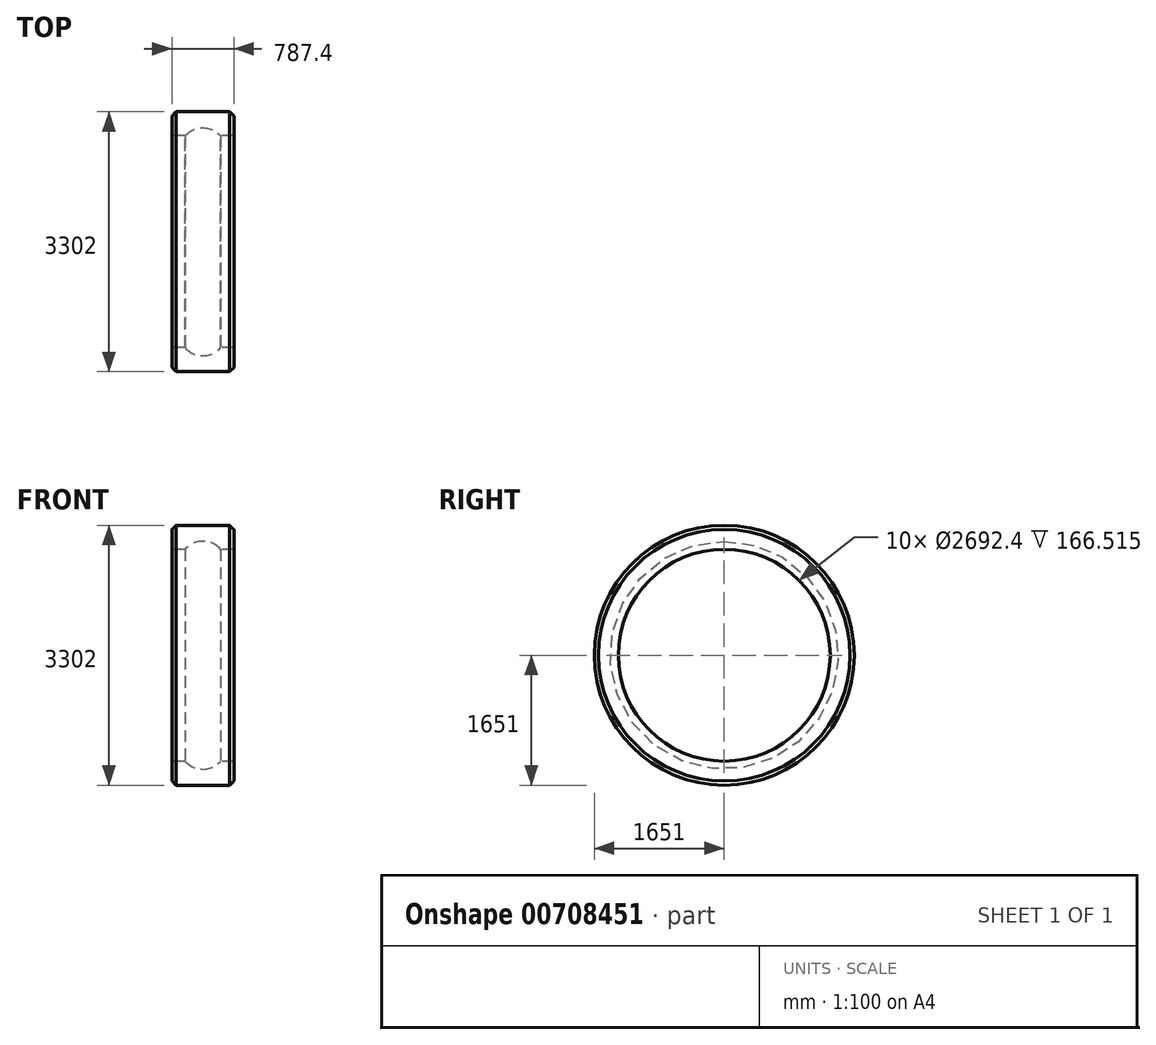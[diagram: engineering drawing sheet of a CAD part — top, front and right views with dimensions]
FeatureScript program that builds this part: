
annotation { "Feature Type Name" : "Feature", "Feature Type Description" : "" }
export const myFeature = defineFeature(function(context is Context, id is Id, definition is map)
    precondition{}
    {
        {
            var Q0;
            Q0=qCreatedBy(makeId("Front.planeOp"),FACE);
            var sketch = newSketch(context, id + "F0", { "sketchPlane" : qUnion([Q0])});
            skLineSegment(sketch, "E0", {"start": v(-565.35, 0) * mm, "end": v(3267.77, 0) * mm});
            skLineSegment(sketch, "E1.bottom", {"start": v(-393.7, 1346.2) * mm, "end": v(-227.18, 1346.2) * mm});
            skLineSegment(sketch, "E1.top", {"start": v(-393.7, 1651) * mm, "end": v(393.7, 1651) * mm});
            skLineSegment(sketch, "E1.left", {"start": v(-393.7, 1346.2) * mm, "end": v(-393.7, 1651) * mm});
            skLineSegment(sketch, "E1.right", {"start": v(393.7, 1346.2) * mm, "end": v(393.7, 1651) * mm});
            skPoint(sketch, "E1.middle", {"position": v(0, 1498.6) * mm});
            skLineSegment(sketch, "E2", {"start": v(0, 1346.2) * mm, "end": v(0, 0) * mm});
            skArc(sketch, "E3", {"start": v(227.18, 1346.2) * mm, "mid": v(0, 1447.8) * mm, "end": v(-227.18, 1346.2) * mm});
            skLineSegment(sketch, "E4.trimOffspring", {"start": v(227.18, 1346.2) * mm, "end": v(393.7, 1346.2) * mm});
            skSolve(sketch);
        }
        {
            var Q0;
            Q0 = qSketchRegion(id + "F0", true);
            var Q1;
            Q1=sQuery(id+"F0.wireOp",EDGE,"E0");
            revolve(context, id + "F1", {"surfaceOperationType" : NewSurfaceOperationType.NEW, "entities" : qUnion([Q0]), "axis" : qUnion([Q1]), "revolveType" : RevolveType.FULL});
        }
        {
            var Q0;
            Q0=makeQuery(id+"F1.opRevolve","SWEPT_FACE",FACE,{"disambiguationData":[OSD([sQuery(id+"F0.wireOp",EDGE,"E1.top")])]});
            chamfer(context, id + "F2", {"entities" : qUnion([Q0]), "width" : 53.34 * mm, "tangentPropagation" : true});
        }
    });
